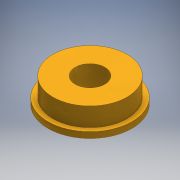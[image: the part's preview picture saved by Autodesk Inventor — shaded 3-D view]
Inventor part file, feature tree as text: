
AUTODESK INVENTOR PART (.ipt)
format: ipt  version: 2020.2 (Build 242310000, 310)  size: 109,056 bytes
history: native  units: mm
features: extrude x2, other x1, sketch x1
ambient origin geometry x8: Origin, YZ Plane, XZ Plane, XY Plane, X Axis, Y Axis, Z Axis, Center Point
bodies: Body1 (feature_tree)
feature tree (4):
  other  "ソリッド1"
  sketch  "スケッチ1"
  extrude  "押し出し1"  Depth=6.0mm
  extrude  "押し出し2"  Depth=15.0mm
